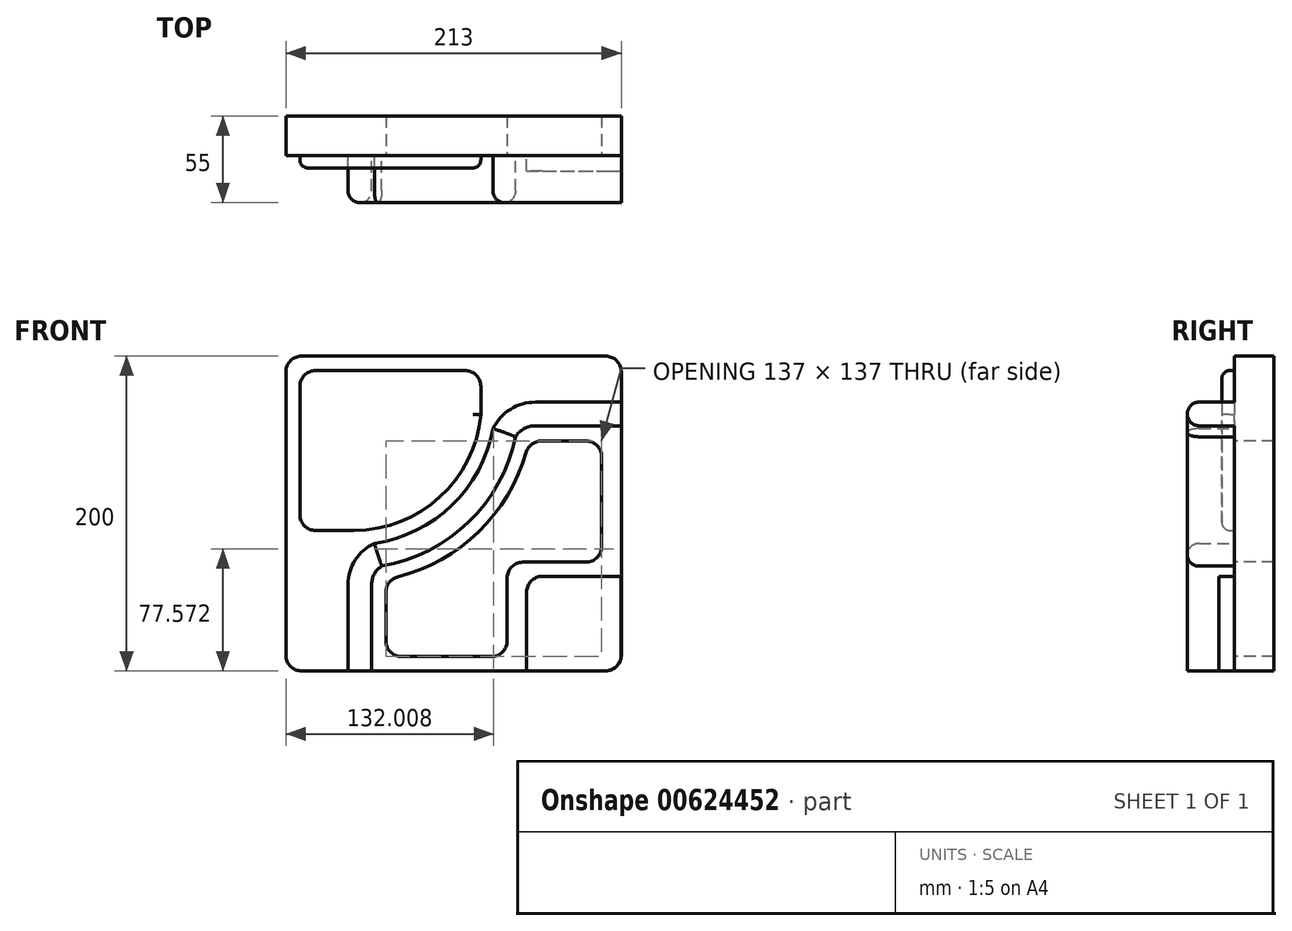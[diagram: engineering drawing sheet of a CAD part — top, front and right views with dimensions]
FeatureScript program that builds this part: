
annotation { "Feature Type Name" : "Feature", "Feature Type Description" : "" }
export const myFeature = defineFeature(function(context is Context, id is Id, definition is map)
    precondition{}
    {
        {
            var Q0;
            Q0=qCreatedBy(makeId("Front.planeOp"),FACE);
            var sketch = newSketch(context, id + "F0", { "sketchPlane" : qUnion([Q0])});
            skLineSegment(sketch, "E0", {"start": v(-106.5, 95) * mm, "end": v(-106.5, -85) * mm});
            skLineSegment(sketch, "E1", {"start": v(-96.5, -95) * mm, "end": v(96.5, -95) * mm});
            skLineSegment(sketch, "E2", {"start": v(106.5, 95) * mm, "end": v(106.5, -85) * mm});
            skLineSegment(sketch, "E3", {"start": v(-96.5, 105) * mm, "end": v(96.5, 105) * mm});
            skPoint(sketch, "E4.visualSharp", {"position": v(-106.5, 105) * mm});
            skArc(sketch, "E4.filletArc", {"start": v(-96.5, 105) * mm, "mid": v(-103.57, 102.07) * mm, "end": v(-106.5, 95) * mm});
            skPoint(sketch, "E5.visualSharp", {"position": v(106.5, 105) * mm});
            skArc(sketch, "E5.filletArc", {"start": v(106.5, 95) * mm, "mid": v(103.57, 102.07) * mm, "end": v(96.5, 105) * mm});
            skPoint(sketch, "E6.visualSharp", {"position": v(106.5, -95) * mm});
            skArc(sketch, "E6.filletArc", {"start": v(96.5, -95) * mm, "mid": v(103.57, -92.07) * mm, "end": v(106.5, -85) * mm});
            skPoint(sketch, "E7.visualSharp", {"position": v(-106.5, -95) * mm});
            skArc(sketch, "E7.filletArc", {"start": v(-106.5, -85) * mm, "mid": v(-103.57, -92.07) * mm, "end": v(-96.5, -95) * mm});
            skSolve(sketch);
        }
        {
            var Q0;
            Q0 = qSketchRegion(id + "F0", true);
            extrude(context, id + "F1", {"entities" : qUnion([Q0]), "depth" : 25 * mm, "offsetDistance" : 25 * mm});
        }
        {
            var Q0;
            Q0=makeQuery(id+"F1.opExtrude","CAP_FACE",FACE,{"disambiguationData":[OSD([sQuery(id+"F0.wireOp",EDGE,"E0"),sQuery(id+"F0.wireOp",EDGE,"E1"),sQuery(id+"F0.wireOp",EDGE,"E2"),sQuery(id+"F0.wireOp",EDGE,"E3"),sQuery(id+"F0.wireOp",EDGE,"E4.filletArc"),sQuery(id+"F0.wireOp",EDGE,"E5.filletArc"),sQuery(id+"F0.wireOp",EDGE,"E6.filletArc"),sQuery(id+"F0.wireOp",EDGE,"E7.filletArc")])],"isStart":false});
            var sketch = newSketch(context, id + "F2", { "sketchPlane" : qUnion([Q0])});
            skArc(sketch, "E8", {"start": v(-50.35, -14.03) * mm, "mid": v(-62.51, -24.57) * mm, "end": v(-67.05, -40) * mm});
            skArc(sketch, "E9", {"start": v(52.02, 75.73) * mm, "mid": v(36.13, 71.18) * mm, "end": v(25.05, 58.9) * mm});
            skLineSegment(sketch, "E10", {"start": v(52.02, 75.73) * mm, "end": v(106.5, 75.73) * mm});
            skLineSegment(sketch, "E11", {"start": v(-67.05, -40) * mm, "end": v(-67.05, -95) * mm});
            skLineSegment(sketch, "E12", {"start": v(-67.05, -95) * mm, "end": v(-52.05, -95) * mm});
            skLineSegment(sketch, "E13", {"start": v(-52.05, -95) * mm, "end": v(-52.05, -40) * mm});
            skLineSegment(sketch, "E14", {"start": v(106.5, 75.73) * mm, "end": v(106.5, 60.73) * mm});
            skLineSegment(sketch, "E15", {"start": v(106.5, 60.73) * mm, "end": v(52.02, 60.73) * mm});
            skArc(sketch, "E16", {"start": v(52.02, 60.73) * mm, "mid": v(44.78, 58.87) * mm, "end": v(39.33, 53.75) * mm});
            skArc(sketch, "E17", {"start": v(-45.6, -28.46) * mm, "mid": v(-50.32, -33.39) * mm, "end": v(-52.05, -40) * mm});
            skArc(sketch, "E18", {"start": v(39.33, 53.75) * mm, "mid": v(9.54, -0.44) * mm, "end": v(-45.6, -28.46) * mm});
            skPoint(sketch, "E18.startSnap0", {"position": v(40.93, 55.85) * mm});
            skPoint(sketch, "E19.orphan", {"position": v(40.93, 64.1) * mm});
            skArc(sketch, "E20", {"start": v(25.05, 58.9) * mm, "mid": v(-0.92, 10.31) * mm, "end": v(-50.35, -14.03) * mm});
            skPoint(sketch, "E21.orphan", {"position": v(-38.5, -11.46) * mm});
            skPoint(sketch, "E22.orphan", {"position": v(-63.5, -15) * mm});
            skPoint(sketch, "E23.orphan", {"position": v(26.5, 75) * mm});
            skPoint(sketch, "E24.trimOffspring.end.orphan", {"position": v(22, 45.7) * mm});
            skSolve(sketch);
        }
        {
            var Q0;
            Q0 = qSketchRegion(id + "F2", true);
            extrude(context, id + "F3", {"entities" : qUnion([Q0]), "operationType" : NewBodyOperationType.ADD, "depth" : 30 * mm, "offsetDistance" : 25 * mm});
        }
        {
            var Q0;
            Q0=makeQuery(id+"F3.opExtrude","CAP_EDGE",EDGE,{"disambiguationData":[OSD([sQuery(id+"F2.wireOp",EDGE,"E11")])],"isStart":false});
            var Q1;
            Q1=makeQuery(id+"F3.opExtrude","CAP_EDGE",EDGE,{"disambiguationData":[OSD([sQuery(id+"F2.wireOp",EDGE,"E8")])],"isStart":false});
            var Q2;
            Q2=makeQuery(id+"F3.opExtrude","CAP_EDGE",EDGE,{"disambiguationData":[OSD([sQuery(id+"F2.wireOp",EDGE,"E20")])],"isStart":false});
            var Q3;
            Q3=makeQuery(id+"F3.opExtrude","CAP_EDGE",EDGE,{"disambiguationData":[OSD([sQuery(id+"F2.wireOp",EDGE,"E9")])],"isStart":false});
            var Q4;
            Q4=makeQuery(id+"F3.opExtrude","CAP_EDGE",EDGE,{"disambiguationData":[OSD([sQuery(id+"F2.wireOp",EDGE,"E10")])],"isStart":false});
            fillet(context, id + "F4", {"entities" : qUnion([Q0, Q1, Q2, Q3, Q4]), "radius" : 7.5 * mm, "tangentPropagation" : true, "allowEdgeOverflow" : false});
        }
        {
            var Q0;
            Q0=makeQuery(id+"F3.opExtrude","CAP_EDGE",EDGE,{"disambiguationData":[OSD([sQuery(id+"F2.wireOp",EDGE,"E13")])],"isStart":false});
            var Q1;
            Q1=makeQuery(id+"F3.opExtrude","CAP_EDGE",EDGE,{"disambiguationData":[OSD([sQuery(id+"F2.wireOp",EDGE,"E17")])],"isStart":false});
            var Q2;
            Q2=makeQuery(id+"F3.opExtrude","CAP_EDGE",EDGE,{"disambiguationData":[OSD([sQuery(id+"F2.wireOp",EDGE,"E18")])],"isStart":false});
            var Q3;
            Q3=makeQuery(id+"F3.opExtrude","CAP_EDGE",EDGE,{"disambiguationData":[OSD([sQuery(id+"F2.wireOp",EDGE,"E16")])],"isStart":false});
            var Q4;
            Q4=makeQuery(id+"F3.opExtrude","CAP_EDGE",EDGE,{"disambiguationData":[OSD([sQuery(id+"F2.wireOp",EDGE,"E15")])],"isStart":false});
            fillet(context, id + "F5", {"entities" : qUnion([Q0, Q1, Q2, Q3, Q4]), "radius" : 7.5 * mm, "tangentPropagation" : true, "allowEdgeOverflow" : false});
        }
        {
            var Q0;
            Q0=makeQuery(id+"F2.imprint","IMPRINT",FACE,{"disambiguationData":[TD([[makeQuery(id+"F2.imprint","IMPRINT",EDGE,{"derivedFrom":sQuery(id+"F2.wireOp",EDGE,"E8")}),-1.0]])]});
            var sketch = newSketch(context, id + "F6", { "sketchPlane" : qUnion([Q0])});
            skArc(sketch, "E25", {"start": v(17.3, 67.77) * mm, "mid": v(-8.78, 15.38) * mm, "end": v(-63.35, -5.77) * mm});
            skLineSegment(sketch, "E26", {"start": v(7.3, 95.81) * mm, "end": v(-87.58, 95.81) * mm});
            skLineSegment(sketch, "E27", {"start": v(-97.58, 85.81) * mm, "end": v(-97.58, 4.23) * mm});
            skLineSegment(sketch, "E28", {"start": v(-87.58, -5.77) * mm, "end": v(-63.35, -5.77) * mm});
            skLineSegment(sketch, "E29", {"start": v(17.3, 85.81) * mm, "end": v(17.3, 67.77) * mm});
            skPoint(sketch, "E30.visualSharp", {"position": v(-97.58, -5.77) * mm});
            skArc(sketch, "E30.filletArc", {"start": v(-97.58, 4.23) * mm, "mid": v(-94.65, -2.84) * mm, "end": v(-87.58, -5.77) * mm});
            skPoint(sketch, "E31.visualSharp", {"position": v(-97.58, 95.81) * mm});
            skArc(sketch, "E31.filletArc", {"start": v(-87.58, 95.81) * mm, "mid": v(-94.65, 92.88) * mm, "end": v(-97.58, 85.81) * mm});
            skPoint(sketch, "E32.visualSharp", {"position": v(17.3, 95.81) * mm});
            skArc(sketch, "E32.filletArc", {"start": v(17.3, 85.81) * mm, "mid": v(14.37, 92.88) * mm, "end": v(7.3, 95.81) * mm});
            skSolve(sketch);
        }
        {
            var Q0;
            Q0 = qSketchRegion(id + "F6", true);
            extrude(context, id + "F7", {"entities" : qUnion([Q0]), "operationType" : NewBodyOperationType.ADD, "depth" : 8 * mm, "offsetDistance" : 25 * mm});
        }
        {
            var Q0;
            Q0=makeQuery(id+"F7.opExtrude","CAP_EDGE",EDGE,{"disambiguationData":[OSD([sQuery(id+"F6.wireOp",EDGE,"E27")])],"isStart":false});
            var Q1;
            Q1=makeQuery(id+"F7.opExtrude","CAP_EDGE",EDGE,{"disambiguationData":[OSD([sQuery(id+"F6.wireOp",EDGE,"E31.filletArc")])],"isStart":false});
            fillet(context, id + "F8", {"entities" : qUnion([Q0, Q1]), "radius" : 5 * mm, "tangentPropagation" : true, "allowEdgeOverflow" : false});
        }
        {
            var Q0;
            {var subQ2=sQuery(id+"F2.wireOp",EDGE,"E13");Q0=makeQuery(id+"F2.imprint","IMPRINT",FACE,{"disambiguationData":[TD([[makeQuery(id+"F2.imprint","IMPRINT",EDGE,{"derivedFrom":subQ2}),-1.0]])]});}
            var sketch = newSketch(context, id + "F9", { "sketchPlane" : qUnion([Q0])});
            skLineSegment(sketch, "E33", {"start": v(-33, -85.93) * mm, "end": v(24, -85.93) * mm});
            skLineSegment(sketch, "E34", {"start": v(44, -25.93) * mm, "end": v(84, -25.93) * mm});
            skLineSegment(sketch, "E35", {"start": v(34, -35.93) * mm, "end": v(34, -75.93) * mm});
            skLineSegment(sketch, "E36", {"start": v(94, -15.93) * mm, "end": v(94, 41.07) * mm});
            skArc(sketch, "E37", {"start": v(46.16, 43.83) * mm, "mid": v(15.92, -6.62) * mm, "end": v(-35.45, -35.28) * mm});
            skLineSegment(sketch, "E38", {"start": v(84, 51.07) * mm, "end": v(55.77, 51.07) * mm});
            skLineSegment(sketch, "E39", {"start": v(-43, -75.93) * mm, "end": v(-43, -44.97) * mm});
            skPoint(sketch, "E40.visualSharp", {"position": v(-43, -85.93) * mm});
            skArc(sketch, "E40.filletArc", {"start": v(-43, -75.93) * mm, "mid": v(-40.06, -83) * mm, "end": v(-33, -85.93) * mm});
            skPoint(sketch, "E41.visualSharp", {"position": v(-43, -36.92) * mm});
            skArc(sketch, "E41.filletArc", {"start": v(-35.45, -35.28) * mm, "mid": v(-40.88, -38.83) * mm, "end": v(-43, -44.97) * mm});
            skPoint(sketch, "E42.visualSharp", {"position": v(34, -85.93) * mm});
            skArc(sketch, "E42.filletArc", {"start": v(24, -85.93) * mm, "mid": v(31.08, -83) * mm, "end": v(34, -75.93) * mm});
            skPoint(sketch, "E43.visualSharp", {"position": v(34, -25.93) * mm});
            skArc(sketch, "E43.filletArc", {"start": v(44, -25.93) * mm, "mid": v(36.94, -28.86) * mm, "end": v(34, -35.93) * mm});
            skPoint(sketch, "E44.visualSharp", {"position": v(94, -25.93) * mm});
            skArc(sketch, "E44.filletArc", {"start": v(84, -25.93) * mm, "mid": v(91.08, -23) * mm, "end": v(94, -15.93) * mm});
            skPoint(sketch, "E45.visualSharp", {"position": v(94, 51.07) * mm});
            skArc(sketch, "E45.filletArc", {"start": v(94, 41.07) * mm, "mid": v(91.08, 48.14) * mm, "end": v(84, 51.07) * mm});
            skPoint(sketch, "E46.visualSharp", {"position": v(47.98, 51.07) * mm});
            skArc(sketch, "E46.filletArc", {"start": v(55.77, 51.07) * mm, "mid": v(49.76, 49.06) * mm, "end": v(46.16, 43.83) * mm});
            skSolve(sketch);
        }
        {
            var Q0;
            Q0 = qSketchRegion(id + "F9", true);
            extrude(context, id + "F10", {"entities" : qUnion([Q0]), "operationType" : NewBodyOperationType.REMOVE, "oppositeDirection" : true, "depth" : 25 * mm, "offsetDistance" : 25 * mm});
        }
        {
            var Q0;
            {var subQ2=sQuery(id+"F2.wireOp",EDGE,"E13");Q0=makeQuery(id+"F2.imprint","IMPRINT",FACE,{"disambiguationData":[TD([[makeQuery(id+"F2.imprint","IMPRINT",EDGE,{"derivedFrom":subQ2}),-1.0]])]});}
            var sketch = newSketch(context, id + "F11", { "sketchPlane" : qUnion([Q0])});
            skLineSegment(sketch, "E47", {"start": v(56.4, -34.92) * mm, "end": v(106.4, -34.92) * mm});
            skLineSegment(sketch, "E48", {"start": v(46.4, -94.92) * mm, "end": v(96.4, -94.92) * mm});
            skLineSegment(sketch, "E49", {"start": v(106.4, -34.92) * mm, "end": v(106.4, -84.92) * mm});
            skLineSegment(sketch, "E50", {"start": v(46.4, -44.92) * mm, "end": v(46.4, -94.92) * mm});
            skPoint(sketch, "E51.visualSharp", {"position": v(46.4, -34.92) * mm});
            skArc(sketch, "E51.filletArc", {"start": v(56.4, -34.92) * mm, "mid": v(49.33, -37.85) * mm, "end": v(46.4, -44.92) * mm});
            skPoint(sketch, "E52.visualSharp", {"position": v(106.4, -94.92) * mm});
            skArc(sketch, "E52.filletArc", {"start": v(96.4, -94.92) * mm, "mid": v(103.47, -92) * mm, "end": v(106.4, -84.92) * mm});
            skSolve(sketch);
        }
        {
            var Q0;
            Q0 = qSketchRegion(id + "F11", true);
            extrude(context, id + "F12", {"entities" : qUnion([Q0]), "operationType" : NewBodyOperationType.ADD, "depth" : 10 * mm, "offsetDistance" : 25 * mm});
        }
    });
